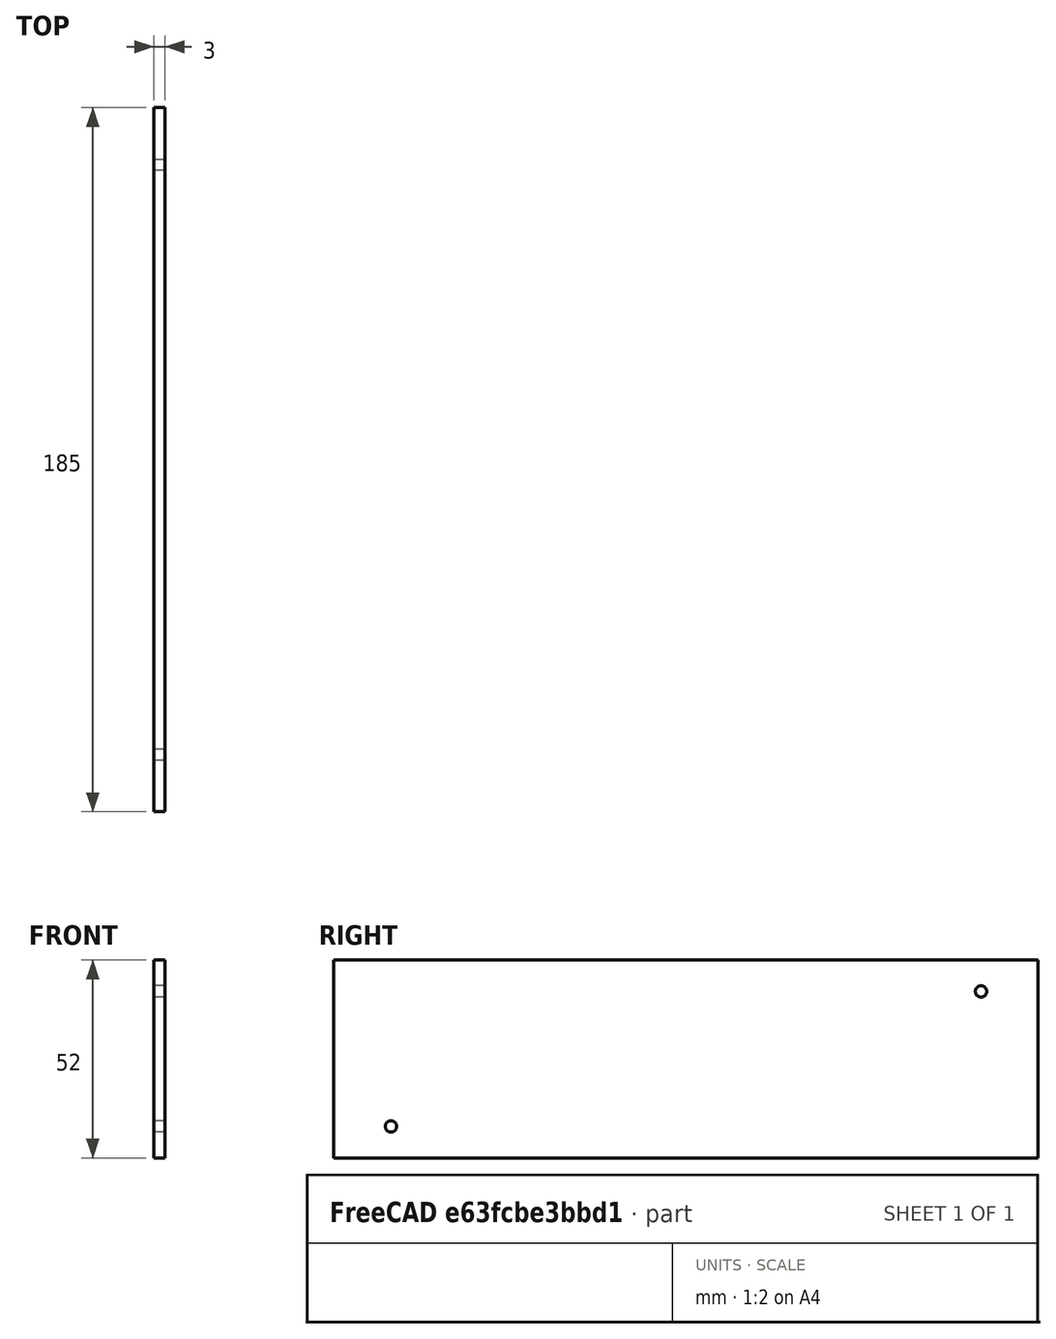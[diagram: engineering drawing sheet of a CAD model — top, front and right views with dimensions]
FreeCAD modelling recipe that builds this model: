
FCSTD DOCUMENT  (FreeCAD 0.20R29410 (Git))
Label: case-back-panel
License: All rights reserved
LicenseURL: http://en.wikipedia.org/wiki/All_rights_reserved
objects: Sketcher::SketchObject×1, PartDesign::Pad×1, PartDesign::Body×1
note: 4 computed .brp shape members not serialized (recipe doc carries the construction recipe); baked Part::Feature solids carry a one-line shape summary decoded from their .brp

FEATURE [Sketcher::SketchObject] Sketch  label="skBase"
  FullyConstrained = true
  MapMode = 5
  Placement = pos=(0,0,0) rot=(0.57735,0.57735,0.57735;2.0944rad)
  Support = -> [YZ_Plane]
  sketch-geometry (12):
    g0: LineSegment StartX=-92.5 StartY=26 StartZ=0 EndX=92.5 EndY=26 EndZ=0
    g1: LineSegment StartX=92.5 StartY=26 StartZ=0 EndX=92.5 EndY=-26 EndZ=0
    g2: LineSegment StartX=92.5 StartY=-26 StartZ=0 EndX=-92.5 EndY=-26 EndZ=0
    g3: LineSegment StartX=-92.5 StartY=-26 StartZ=0 EndX=-92.5 EndY=26 EndZ=0
    g4: LineSegment StartX=-81 StartY=21.25 StartZ=0 EndX=81 EndY=21.25 EndZ=0
    g5: LineSegment StartX=81 StartY=21.25 StartZ=0 EndX=81 EndY=-21.25 EndZ=0
    g6: LineSegment StartX=81 StartY=-21.25 StartZ=0 EndX=-81 EndY=-21.25 EndZ=0
    g7: LineSegment StartX=-81 StartY=-21.25 StartZ=0 EndX=-81 EndY=21.25 EndZ=0
    g8: Circle CenterX=-77.5 CenterY=-17.75 CenterZ=0 NormalX=0 NormalY=0 NormalZ=1 AngleXU=0 Radius=3.5
    g9: Circle CenterX=77.5 CenterY=17.75 CenterZ=0 NormalX=0 NormalY=0 NormalZ=1 AngleXU=0 Radius=3.5
    g10: Circle CenterX=-77.5 CenterY=-17.75 CenterZ=0 NormalX=0 NormalY=0 NormalZ=1 AngleXU=0 Radius=1.5
    g11: Circle CenterX=77.5 CenterY=17.75 CenterZ=0 NormalX=0 NormalY=0 NormalZ=1 AngleXU=0 Radius=1.5
  constraints (31):
    c: Coincident(g0,g1)
    c: Coincident(g2,g3)
    c: Coincident(g3,g0)
    c: Horizontal(g2)
    c: Vertical(g3)
    c: Distance(g1) = 52
    c: Coincident(g2,g1)
    c: Symmetric(g0,g0,g-2)
    c: Distance(g0) = 185
    c: Symmetric(g0,g1,g-1)
    c: Coincident(g4,g5)
    c: Coincident(g5,g6)
    c: Coincident(g6,g7)
    c: Coincident(g7,g4)
    c: Horizontal(g4)
    c: Horizontal(g6)
    c: Vertical(g5)
    c: Vertical(g7)
    c: Distance(g4) = 162
    c: Distance(g5) = 42.5
    c: Tangent(g9,g5)
    c: Tangent(g9,g4)
    c: Tangent(g8,g6)
    c: Tangent(g8,g7)
    c: Equal(g9,g8)
    c: Radius(g9) = 3.5
    c: Coincident(g10,g8)
    c: Coincident(g9,g11)
    c: Equal(g11,g10)
    c: Diameter(g11) = 3
    c: Symmetric(g10,g11,g-1)
FEATURE [PartDesign::Pad] Pad  label="pdBase"
  Direction = (1,-2e-16,3e-16)
  Length = 3
  Length2 = 10
  Placement = pos=(0,0,0) rot=(0.57735,0.57735,0.57735;2.0944rad)
  Profile = -> Sketch
  ReferenceAxis = -> Sketch [N_Axis]
  Type = 0
FEATURE [PartDesign::Body] Body
  Group = -> [Sketch,Pad]
  Origin = -> Origin
  Tip = -> Pad
